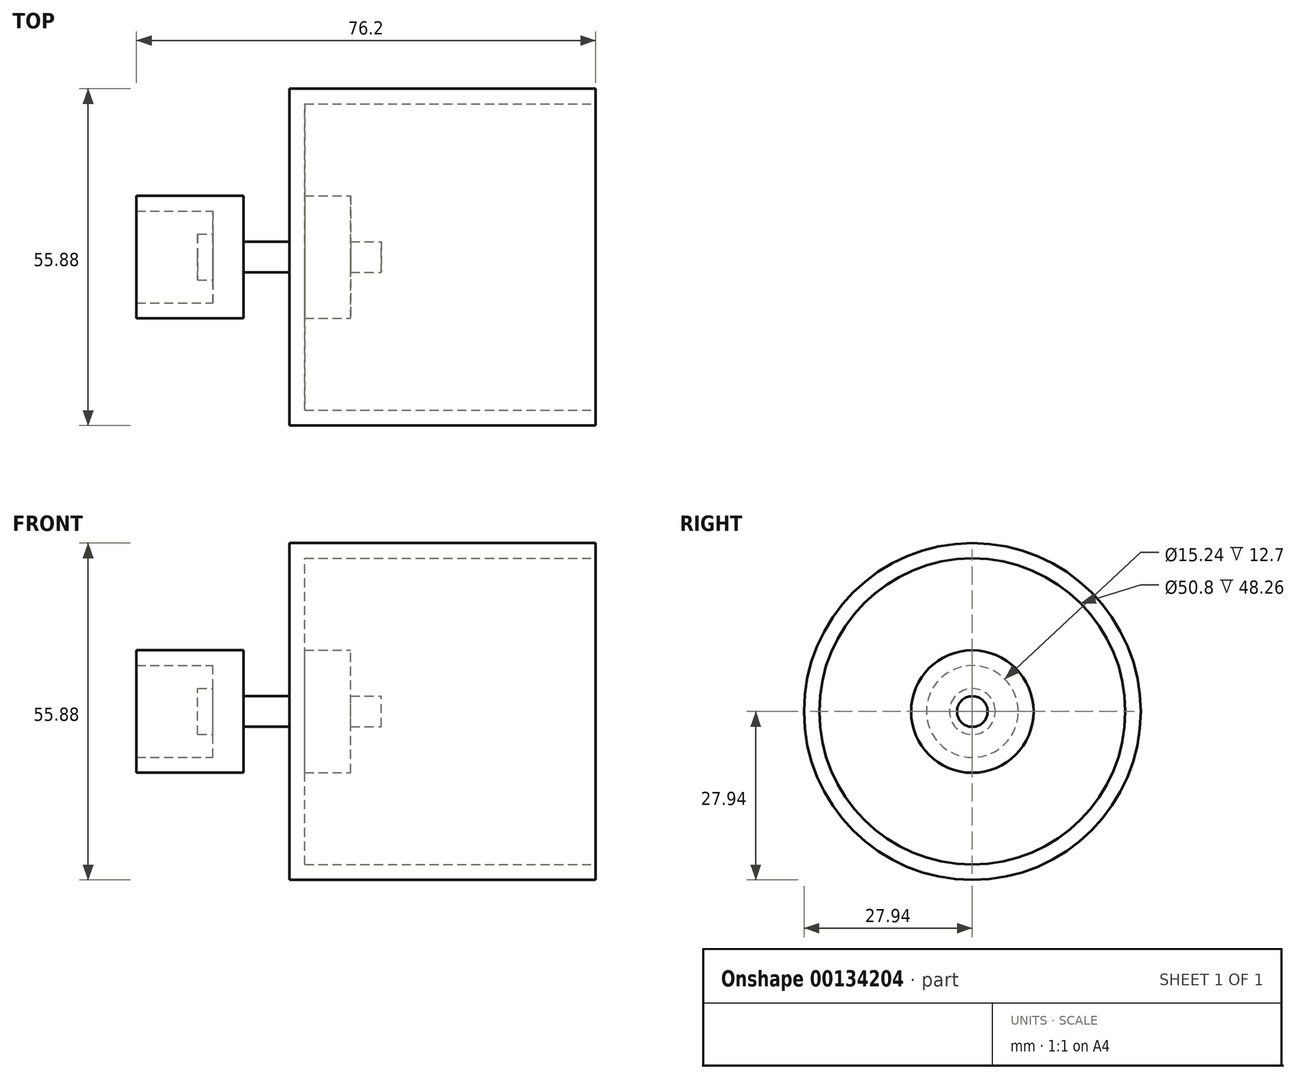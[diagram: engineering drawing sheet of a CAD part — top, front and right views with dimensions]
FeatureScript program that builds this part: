
annotation { "Feature Type Name" : "Feature", "Feature Type Description" : "" }
export const myFeature = defineFeature(function(context is Context, id is Id, definition is map)
    precondition{}
    {
        {
            var Q0;
            Q0=qCreatedBy(makeId("Top.planeOp"),FACE);
            var sketch = newSketch(context, id + "F0", { "sketchPlane" : qUnion([Q0])});
            skLineSegment(sketch, "E0", {"start": v(0, 10.16) * mm, "end": v(5.08, 10.16) * mm});
            skLineSegment(sketch, "E1", {"start": v(5.08, 10.16) * mm, "end": v(5.08, 2.54) * mm});
            skLineSegment(sketch, "E2", {"start": v(5.08, 2.54) * mm, "end": v(12.7, 2.54) * mm});
            skLineSegment(sketch, "E3", {"start": v(12.7, 2.54) * mm, "end": v(12.7, 27.94) * mm});
            skLineSegment(sketch, "E4", {"start": v(12.7, 27.94) * mm, "end": v(63.5, 27.94) * mm});
            skLineSegment(sketch, "E5", {"start": v(63.5, 27.94) * mm, "end": v(63.5, 25.4) * mm});
            skLineSegment(sketch, "E6", {"start": v(63.5, 25.4) * mm, "end": v(15.24, 25.4) * mm});
            skLineSegment(sketch, "E7", {"start": v(15.24, 0) * mm, "end": v(0, 0) * mm});
            skLineSegment(sketch, "E8", {"start": v(27.94, 0) * mm, "end": v(15.24, 0) * mm});
            skLineSegment(sketch, "E9", {"start": v(0, 10.16) * mm, "end": v(-12.7, 10.16) * mm});
            skLineSegment(sketch, "E10", {"start": v(-12.7, 10.16) * mm, "end": v(-12.7, 7.62) * mm});
            skLineSegment(sketch, "E11", {"start": v(0, 7.62) * mm, "end": v(0, 3.8) * mm});
            skLineSegment(sketch, "E12", {"start": v(0, 3.8) * mm, "end": v(-2.54, 3.8) * mm});
            skLineSegment(sketch, "E13", {"start": v(-2.54, 3.8) * mm, "end": v(-2.54, 0) * mm});
            skLineSegment(sketch, "E14", {"start": v(-2.54, 0) * mm, "end": v(0, 0) * mm});
            skLineSegment(sketch, "E15", {"start": v(-12.7, 7.62) * mm, "end": v(0, 7.62) * mm});
            skLineSegment(sketch, "E16", {"start": v(27.94, 0) * mm, "end": v(27.94, 2.54) * mm});
            skLineSegment(sketch, "E17", {"start": v(27.94, 2.54) * mm, "end": v(22.86, 2.54) * mm});
            skLineSegment(sketch, "E18", {"start": v(22.86, 2.54) * mm, "end": v(22.86, 10.16) * mm});
            skLineSegment(sketch, "E19", {"start": v(22.86, 10.16) * mm, "end": v(15.24, 10.16) * mm});
            skLineSegment(sketch, "E20", {"start": v(15.24, 25.4) * mm, "end": v(15.24, 10.16) * mm});
            skSolve(sketch);
        }
        {
            var Q0;
            Q0=makeQuery(id+"F0.imprint","IMPRINT",FACE,{"disambiguationData":[TD([[makeQuery(id+"F0.imprint","IMPRINT",EDGE,{"derivedFrom":sQuery(id+"F0.wireOp",EDGE,"E0")}),-1.0]])]});
            var Q1;
            Q1=sQuery(id+"F0.wireOp",EDGE,"E7");
            revolve(context, id + "F1", {"entities" : qUnion([Q0]), "axis" : qUnion([Q1]), "revolveType" : RevolveType.FULL});
        }
    });
